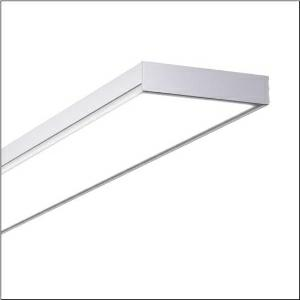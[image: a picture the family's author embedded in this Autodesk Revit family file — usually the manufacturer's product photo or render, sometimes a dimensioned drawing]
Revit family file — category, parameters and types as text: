
# Revit family: apollon_r__31_surface_51mp26wd2341e_c239
name_source: partatom
category: Lighting Fixtures
units: mm (PartAtom-declared; Revit-internal decimal feet)

## family parameters
Cut with Voids When Loaded = No
Host = Face
Light Source = No
Part Type = Normal
Room Calculation Point = No
Round Connector Dimension = Use Diameter
Shared = No

## types (1)
- Apollon® 31 Surface (1 x LED, 4400 lm, 33 W, 3000K)
    Apparent Load = 33 VA
    CIE Flux Codes = 61 87 97 97 100
    Color Rendering = 80
    Color Temperature = 3000K
    Default Elevation = 1800 mm
    Description = Apollon® 31 Surface, office luminaire, primary optical cover: micro prismatic cover, of PMMA, light emission: direct distribution, primary light characteristic: symmetric, installation type: surface-mounted, LED, rated luminous flux: 4.400lm, luminous efficacy: 133lm/W, light colour: 830, colour temperature: 3000K, control gear: DALI 2, with terminal, 5-pole, mains connection: 220..240V, AC, 50/60Hz, rated input power: 33W, housing, of sheet steel, coil coated, metallic grey (RAL 9006), length: 1.545mm, width: 200mm, height: 44mm, protection rating (complete): IP20, insulation class (complete): insulation class II (safety insulation), certification: CE, impact resistance: IK02, permissible operating ambient temperature: -20..+40°C, standard: EN 60598-2-22, packaging unit: 1 piece
    Height = 44 mm
    Lamp = 1 x LED
    Lamp Light Flux = 4400 lm
    Lamp Power = 33 W
    Lamp count = 1
    Length = 1545 mm
    Luminous efficacy = 133 lm/W
    Manufacturer = Siteco
    ModVariant = No
    Model = 51MP26WD2341E
    Mounting Place = Ceiling
    Mounting Type = Surface mounted
    Number of Poles = 1
    OnlyDefault = Yes
    Power Factor = 1
    Product Name = Apollon® 31 Surface
    Product group = office luminaire | ceiling mounted
    ProductGroupID = 302
    Protection Class = Protection class II
    Protection Degree = IP 20
    RLX_Detail_Level = 1
    RLX_Emergency_Light_Flux = 0 lm
    RLX_Emergency_Type = 0
    RLX_Emergency_Type_DB = No
    RlxData = <blob elided: 24085 chars, md5=945b91e9>
    Socket = socket
    Standby Power = 0 W
    System Light Flux = 4400 lm
    System Power = 33 W
    Type Comments = Product without accessories
    Type Image = l_1313654.jpg
    URL = http://relux.com
    VarID = ---
    Voltage = 0 V
    Weight = 0.00 kg
    Width = 200 mm  [stored 0.656168 ft]

note: [stored X ft] marks values corroborated as IEEE doubles in the binary element streams (Revit-internal decimal feet)

## geometry (parser evidence)
native form markers: Blend x4, Sweep x12
no freeform markers — native parametric forms only
